# Revit family: IS_Connect2_K9271_BIM_IT
name_source: partatom
category: Plumbing Fixtures
units: mm (PartAtom-declared; Revit-internal decimal feet)

## family parameters
Always vertical = No
Cut with Voids When Loaded = No
OmniClass Number = 23.45.05.14.21.11
OmniClass Title = Bath/Shower Units
Part Type = Normal
Room Calculation Point = No
Round Connector Dimension = Use Diameter
Shared = No
Work Plane-Based = No

## types (2) — shared parameters
Accessori = https://www.idealstandard.it
Aiuto = https://www.idealstandard.it
AltezzaNominale = 1950 mm  [stored 6.39764 ft]
Autore = Ideal Standard
BIMobject category = Shower screens
BIMobject category code = sanitary-shower-screens
BIMobject main category = Sanitary
BIMobject main category code = sanitary
Brand = Ideal Standard
Brand url = http://www.idealstandard.it
Caratteristiche = CONNECT 2, PORTA GIREVOLE 95 VETRO TRASPARENTE
Description = Porta doccia con anta pivotante, vetro temperato di 6 mm, trattamento Ideal Clean e finitura profili brillante. Apertura pivotante, chiusura magnética e installazione reversibile.
DescrizioneClassifcazioneUni2015 = Shower enclosures
Desrizione = Porta doccia con anta pivotante, vetro temperato di 6 mm, trattamento Ideal Clean e finitura profili brillante. Apertura pivotante, chiusura magnética e installazione reversibile.
Dimensione = 1950 x 0 x 33mm
DurataGaranzia = 2
DurataGaranziaProdotti = 2
Forma = Regtangolare
Garanzia = Garanzia Idealstandard
IFC Classification = Sanitary Terminal
IfcEsportaCome = IfcFurnitureType
InformaziniGaranzia = www.idealstandard.it/garanzia.html
InformazioniDiProdotto = https://www.idealstandard.it
InformazioniGaranzia = www.idealstandard.it/garanzia.html
Installation instructions = https://www.idealstandard.it
InstruzioniInstallazione = https://www.idealstandard.it
LunghezzaNominale = 950 mm
Maniglia = No
Manufacturer = www.idealstandard.it
Manufacturer name = Ideal Standard
Material main = Glass
Materiale = Vetro Temperato
NBS Reference Code = 35-06-79
NBS Reference Description = Shower Enclosures
Nome = ShowerEnclosure_Connect2_K9271_IdealStandard
NomeOggettoBim = ISI_IdealStandard_ShowersEnclosures_Connect2_K9271
Nominal height = 1950
NumeroDiModello = K9271EO
OmniClass Code = 23-31 17 17
OmniClass Description = Shower Enclosures
PartiDiRicambio = https://www.idealstandard.it
PesoNetto = 33
PiattoDoccia = No
Product Guid = f2df7c7f-95f7-434f-a140-08a8e6f62f71
Product SKU = K9271
Product data url = https://bimobject.com
Product family = CONNECT II
Product group = Shower Enclosure
Product url = https://www.idealstandard.it
Produttore = Ideal Standard
QR code = http://bimobject.com
RiferimentoClassificazioneUni2015 = Pr_40_20_06_79
Spazio = Interno
Technical description = https://www.idealstandard.it
Telefono = 800 652 290
TipoEspotazioneIfc = SHOWER
UNSPSC Code = 301815
URL = https://www.idealstandard.it
Uniclass 1.4 Code = L72142
Uniclass 1.4 Description = Shower screens, curtains
Uniclass 2.0 Code = PR-35-06-79
Uniclass 2.0 Description = Shower Enclosures
Uniclass 2015 Code = Pr_40_20_06_79
Uniclass 2015 Name = Shower enclosures
UnitàDurata = Anno
UnitàDurataGaranzia = Anno
UnitàLineare = millimitri
UnitàMonetaria = €
UnitàSuperficie = millimitri
UnitàVolume = Litri
Versione = 1
VersioneClassificazioneUni2015 = v1.20
Weight Net (Kg) = 33
Youtube clip = https://www.youtube.com
zero-valued in all types: CostoDiSostituzione, DimensioneScarico, LarghezzaNominale, Nominal depth, ProfonditaNominale, SeatMaterial, SpessoreDelMateriale, SpilloverLivello

## per-type parameters (varying)
| type | CodiceABarre | Colore | Date of publishing | Edition number | Finitura | GTIN code | Model | ModelloDiRiferimento | Product name | Revisione | Riferimento |
| K9271V3 - CONNECT 2 PIVOT DOOR 95 CLEAR GLASS - MATT BLACK | 8014140483700 | NERO OPACO | 18/05/2021 | 1 | NERO OPACO | https://8014140483700 | K9271V3 | K9271V3 | CONNECT 2, PIVOT DOOR 95 CLEAR GLASS  -  MATT BLACK | 1 | CONNECT 2, PIVOT DOOR 95 CLEAR GLASS  -  MATT BLACK |
| K9271V3 - CONNECT 2 PIVOT DOOR 95 CLEAR GLASS - SILVER | 8014140456100 | ARGENTO | 17/10/2019 | 2 | ARGENTO | https://8014140456100 | K9271EO | K9271EO | CONNECT 2, PIVOT DOOR 95 CLEAR GLASS  -  SILVER | 2 | CONNECT 2, PIVOT DOOR 95 CLEAR GLASS  -  SILVER |

note: [stored X ft] marks values corroborated as IEEE doubles in the binary element streams (Revit-internal decimal feet)

## geometry (parser evidence)
native form markers: Sweep x3
no freeform markers — native parametric forms only
